# Revit family: 55350110(2022)
name_source: partatom
category: Plumbing Fixtures
revit_build: Autodesk Revit 2018 (Build: 20170223_1515(x64)
units: mm (PartAtom-declared; Revit-internal decimal feet)

## family parameters
Always vertical = Yes
Cut with Voids When Loaded = No
OmniClass Number = 23.45.55.00
OmniClass Title = Sanitary Faucets, Wastes
Part Type = Normal
Room Calculation Point = No
Round Connector Dimension = Use Diameter
Shared = No
Work Plane-Based = No

## types (1)
- 55350110 Shower system
    2D/3D/BIM Files URL = http://static.hansa.com
    Advanced Features = Flexible length / can be shortened
    AssetType = Fixed
    BIMObjectName = 55350110(2022)
    Backflow Prevention EN1717 = EB
    BodyMaterial = Brass
    Brand = HANSA
    Catalog Drawing URL = http://static.hansa.com
    CloseOffRating = 0
    Color = Chrome
    Connection = Eccentric coupling(s);Cover plate(s);Silencer(s)
    Connection Size = G1/2
    Dimension Drawing URL = http://static.hansa.com
    Diverter = Turn operated diverter;Integrated into flow control handle
    DurationUnit = Year
    EAN Number = 4057304019197
    EN Standard = EN 1111, EN 1112, EN 1113
    ETIM Class Number = EC010109 Sliding rod combination
    FDV Document URL = http://www.hansa.com
    FaucetMainMaterial = Brass
    Features = Thermostatic
    Finish = Polished
    Flow Drawing URL = http://static.hansa.com
    Flow Rate At 300kPa = 0.3 L/s
    FlowCoefficient = 0
    Group = Shower system
    IfcExportAs = IfcValveType
    IfcExportType = FAUCET
    Installation Type = Wall mounted
    Installation Width = CC150 ± 15 mm
    Installation and Maintenance Guide URL = http://static.hansa.com
    Lever Handle = Temperature control handle;Flow control handle
    Manufacturer = HANSA
    ManufacturerName = HANSA
    ManufacturerURL = http://www.hansa.com
    Market = International;Germany
    Material = Brass
    Max. Hot Water Supply = 65 °C
    Mechanical Parts = Ceramic head part for flow control;Thermostatic cartridge for automatic temperature control;Non-return valve(s);Litter filter(s)
    Mobile Product Information URL = http://mpi.hansa.com
    Model = 55350110 Shower system
    ModelReference = 55350110
    NBSDescription = Shower mixers
    NBSReference = 45-35-70/335
    Name = 55350110 Shower system
    Name_en = 55350110 Shower system
    NominalDepth = 529 mm
    NominalHeight = 1155 mm
    NominalWidth = 290 mm
    Product Code = 55350110
    Product Family = 5160
    Product Image URL = http://static.hansa.com
    Product URL = http://static.hansa.com
    Sales Package dimensions (LxWxH) = 985 x 325 x 100
    Shape = Sculptured
    Shower Parts = Hand shower;Shower rail;Overhead shower;Shower hose (1500 mm);Anti limescale technology (easy to clean)
    Shower Spray Number = 1 shower spray
    ShowerDefaultElevation = 900 mm  [stored 2.95276 ft]
    Size = 290x530x1155 mm
    Surface treatment = Chrome
    Technical DataSheet URL = http://www.hansa.com
    Temperature Adjustments = Safety stop against scalding at 38°C;The housing of the fittings conducts minimal heat
    UNSPSC Class Number = 30181700 Faucets or taps
    URL Declaration of Conformity = http://static.hansa.com
    URL REACH = http://static.hansa.com
    Uniclass2 = Pr_40_30_96_78
    Uniclass2015Description = Shower manual water supply sets
    Uniclass2015Reference = Pr_40_20_87_78
    Version = 1
    VersionDate = 23/11/2022
    Warranty Information URL = http://warranty.hansa.com
    WarrantyDescription = http://warranty.hansa.com
    WarrantyDurationUnit = Year
    Working Pressure = 100 - 1000 kPa

note: [stored X ft] marks values corroborated as IEEE doubles in the binary element streams (Revit-internal decimal feet)

## geometry (parser evidence)
native form markers: Sweep x5
no freeform markers — native parametric forms only
